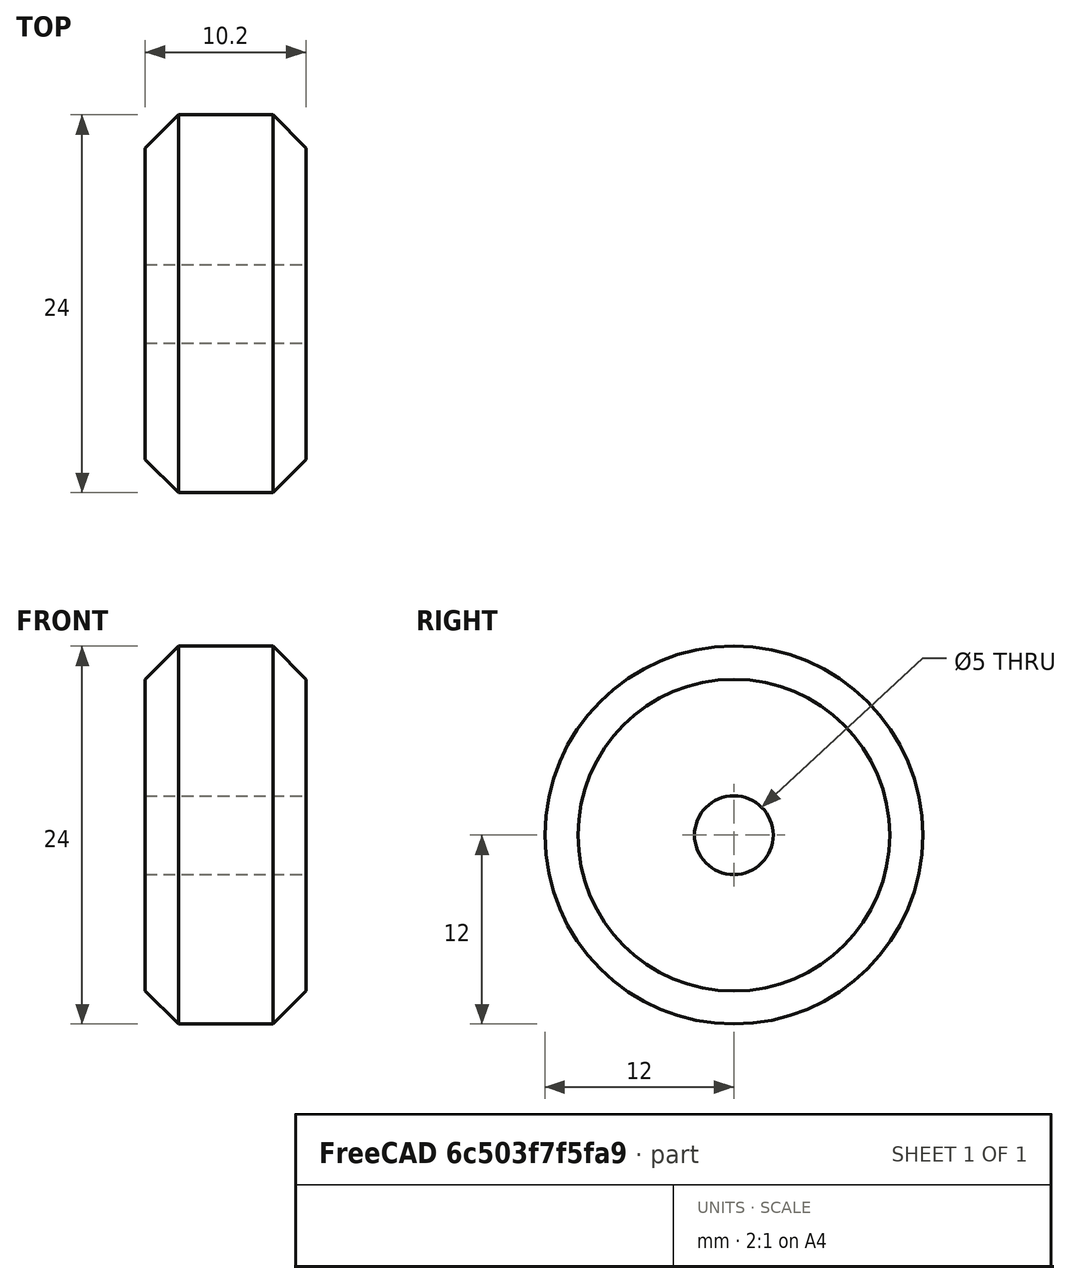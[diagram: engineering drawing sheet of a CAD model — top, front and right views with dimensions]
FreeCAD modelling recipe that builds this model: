
FCSTD DOCUMENT  (FreeCAD 0.18R15969 (Git))
Label: v-slot-wheel
License: All rights reserved
LicenseURL: http://en.wikipedia.org/wiki/All_rights_reserved
objects: Sketcher::SketchObject×1, PartDesign::Revolution×1, PartDesign::Body×1
note: 4 computed .brp shape members not serialized (recipe doc carries the construction recipe); baked Part::Feature solids carry a one-line shape summary decoded from their .brp

FEATURE [Sketcher::SketchObject] Sketch
  MapMode = 5
  Placement = pos=(0,0,0) rot=(1,0,0;1.5708rad)
  Support = -> [XZ_Plane]
  sketch-geometry (8):
    g0: LineSegment StartX=-3 StartY=12 StartZ=0 EndX=-5.1 EndY=9.9 EndZ=0
    g1: LineSegment StartX=-3 StartY=12 StartZ=0 EndX=3 EndY=12 EndZ=0
    g2: LineSegment StartX=3 StartY=12 StartZ=0 EndX=5.1 EndY=9.9 EndZ=0
    g3: LineSegment StartX=-5.1 StartY=9.9 StartZ=0 EndX=-5.1 EndY=2.5 EndZ=0
    g4: LineSegment StartX=-5.1 StartY=2.5 StartZ=0 EndX=5.1 EndY=2.5 EndZ=0
    g5: LineSegment StartX=5.1 StartY=2.5 StartZ=0 EndX=5.1 EndY=9.9 EndZ=0
    g6: LineSegment [constr] StartX=-5.1 StartY=2.5 StartZ=0 EndX=0 EndY=0 EndZ=0
    g7: LineSegment [constr] StartX=0 StartY=0 StartZ=0 EndX=5.1 EndY=2.5 EndZ=0
  constraints (22):
    c: Coincident(g1,g0)
    c: Horizontal(g1)
    c: Coincident(g2,g1)
    c: Coincident(g3,g0)
    c: Vertical(g3)
    c: Coincident(g4,g3)
    c: Horizontal(g4)
    c: Coincident(g5,g4)
    c: Coincident(g5,g2)
    c: Vertical(g5)
    c: Coincident(g6,g3)
    c: Coincident(g6,g-1)
    c: Coincident(g7,g-1)
    c: Coincident(g7,g4)
    c: Equal(g7,g6)
    c: DistanceY(g-1,g3) = 2.5
    c: DistanceX(g3,g4) = 10.2
    c: Equal(g0,g2)
    c: Equal(g3,g5)
    c: Angle(g3,g0) = 2.35619
    c: DistanceX(g1,g1) = 6
    c: DistanceY(g-1,g0) = 12
FEATURE [PartDesign::Revolution] Revolution
  Angle = 360
  Axis = (1,0,0)
  Base = (0,0,0)
  Placement = pos=(0,0,0) rot=(1,0,0;1.5708rad)
  Profile = -> Sketch
  ReferenceAxis = -> X_Axis
  Refine = true
  Reversed = true
FEATURE [PartDesign::Body] Body
  Group = -> [Sketch,Revolution]
  Origin = -> Origin
  Tip = -> Revolution
